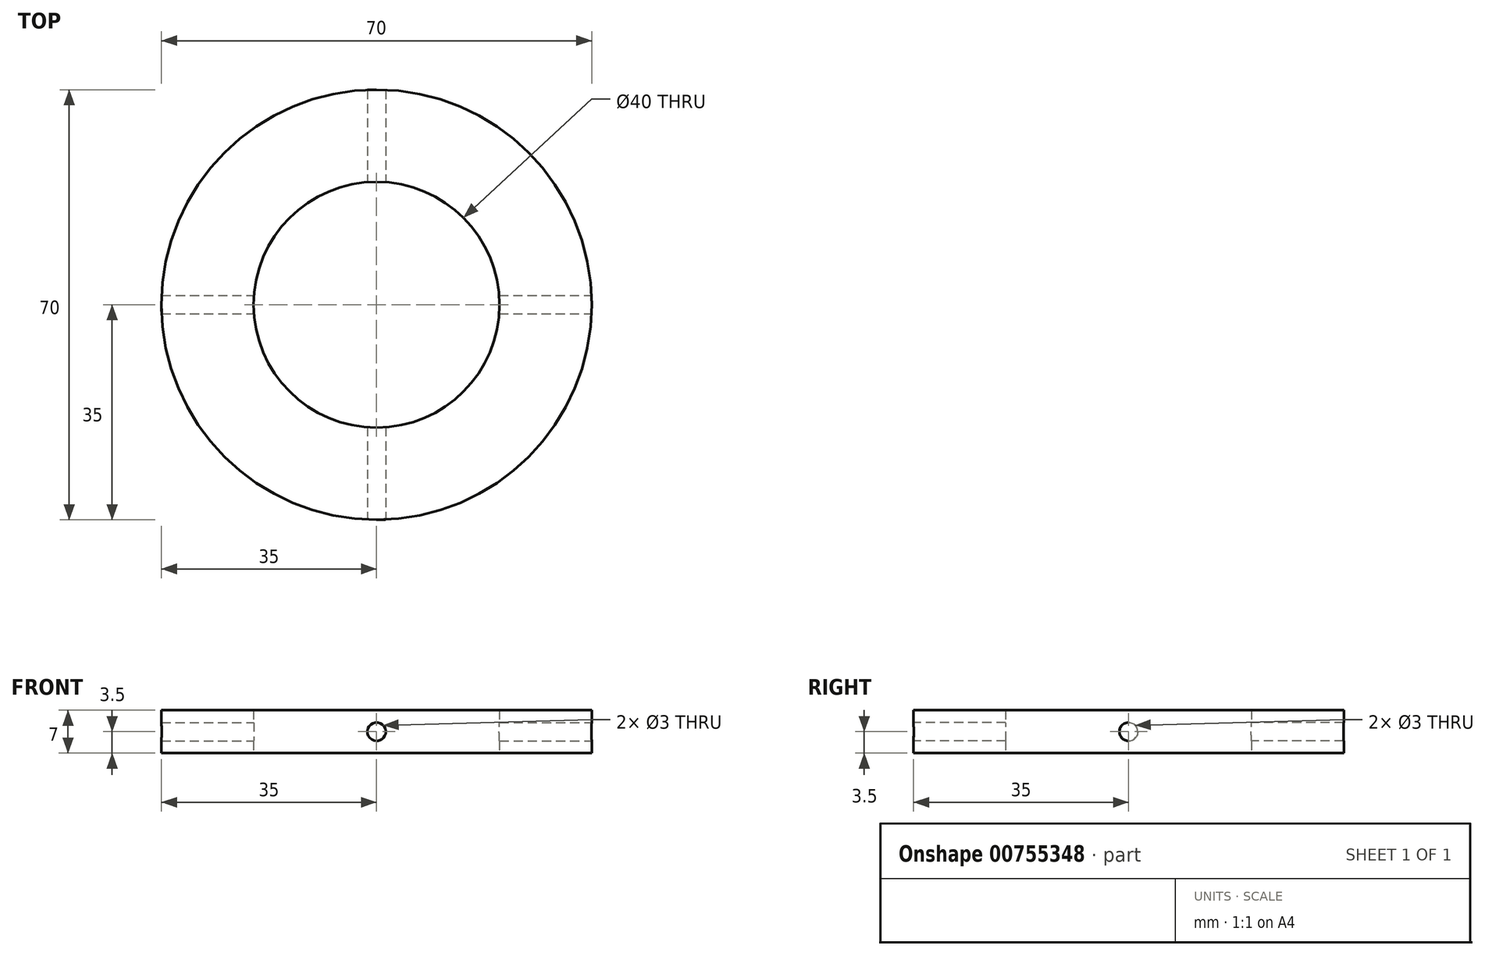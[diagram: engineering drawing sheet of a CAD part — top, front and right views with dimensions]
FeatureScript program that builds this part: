
annotation { "Feature Type Name" : "Feature", "Feature Type Description" : "" }
export const myFeature = defineFeature(function(context is Context, id is Id, definition is map)
    precondition{}
    {
        {
            var Q0;
            Q0=qCreatedBy(makeId("Top.planeOp"),FACE);
            var sketch = newSketch(context, id + "F0", { "sketchPlane" : qUnion([Q0])});
            skLineSegment(sketch, "E0", {"start": v(0, 120) * mm, "end": v(24.29, -18.33) * mm, "construction": true});
            skLineSegment(sketch, "E1", {"start": v(200, 0) * mm, "end": v(-17.1, -22.65) * mm, "construction": true});
            skLineSegment(sketch, "E2", {"start": v(0, -120) * mm, "end": v(-24.29, 18.33) * mm, "construction": true});
            skLineSegment(sketch, "E3", {"start": v(-200, 0) * mm, "end": v(17.1, 22.65) * mm, "construction": true});
            skCircle(sketch, "E4", {"center": v(0, 0) * mm, "radius": 20.75 * mm, "construction": true});
            skCircle(sketch, "E5", {"center": v(0, 0) * mm, "radius": 35 * mm});
            skCircle(sketch, "E6", {"center": v(0, 0) * mm, "radius": 20 * mm});
            skSolve(sketch);
        }
        {
            var Q0;
            Q0 = qSketchRegion(id + "F0", true);
            var Q1;
            Q1=sQuery(id+"F0.wireOp",EDGE,"E3");
            var Q2;
            Q2=sQuery(id+"F0.wireOp",EDGE,"E0");
            var Q3;
            Q3=sQuery(id+"F0.wireOp",EDGE,"E2");
            var Q4;
            Q4=sQuery(id+"F0.wireOp",EDGE,"E1");
            extrude(context, id + "F1", {"entities" : qUnion([Q0]), "surfaceEntities" : qUnion([Q1, Q2, Q3, Q4]), "endBound" : BoundingType.SYMMETRIC, "depth" : 7 * mm, "offsetDistance" : 25 * mm, "hasSecondDirection" : true, "secondDirectionOppositeDirection" : true, "secondDirectionDepth" : 3.5 * mm});
        }
        {
            var Q0;
            Q0=qCreatedBy(makeId("Right.planeOp"),FACE);
            var sketch = newSketch(context, id + "F2", { "sketchPlane" : qUnion([Q0])});
            skCircle(sketch, "E7", {"center": v(0, 0) * mm, "radius": 1.5 * mm});
            skSolve(sketch);
        }
        {
            var Q0;
            Q0=qCreatedBy(makeId("Front.planeOp"),FACE);
            var sketch = newSketch(context, id + "F3", { "sketchPlane" : qUnion([Q0])});
            skCircle(sketch, "E8", {"center": v(0, 0) * mm, "radius": 1.5 * mm});
            skSolve(sketch);
        }
        {
            var Q0;
            Q0 = qSketchRegion(id + "F2", true);
            extrude(context, id + "F4", {"entities" : qUnion([Q0]), "operationType" : NewBodyOperationType.REMOVE, "endBound" : BoundingType.THROUGH_ALL, "oppositeDirection" : true, "depth" : 25 * mm, "offsetDistance" : 25 * mm, "hasSecondDirection" : true, "secondDirectionBound" : SecondDirectionBoundingType.THROUGH_ALL, "secondDirectionOppositeDirection" : false, "secondDirectionDepth" : 25 * mm});
        }
        {
            var Q0;
            Q0 = qSketchRegion(id + "F3", true);
            extrude(context, id + "F5", {"entities" : qUnion([Q0]), "operationType" : NewBodyOperationType.REMOVE, "endBound" : BoundingType.THROUGH_ALL, "oppositeDirection" : true, "depth" : 25 * mm, "offsetDistance" : 25 * mm, "hasSecondDirection" : true, "secondDirectionBound" : SecondDirectionBoundingType.THROUGH_ALL, "secondDirectionOppositeDirection" : false, "secondDirectionDepth" : 25 * mm});
        }
        {
            var Q0;
            Q0=sQuery(id+"F0.wireOp",VERTEX,"E3.start");
            var Q1;
            Q1=sQuery(id+"F0.wireOp",EDGE,"E3");
            cPlane(context, id + "F6", {"entities" : qUnion([Q0, Q1]), "cplaneType" : CPlaneType.LINE_POINT, "offset" : 25 * mm, "width" : 150 * mm, "height" : 150 * mm});
        }
    });
